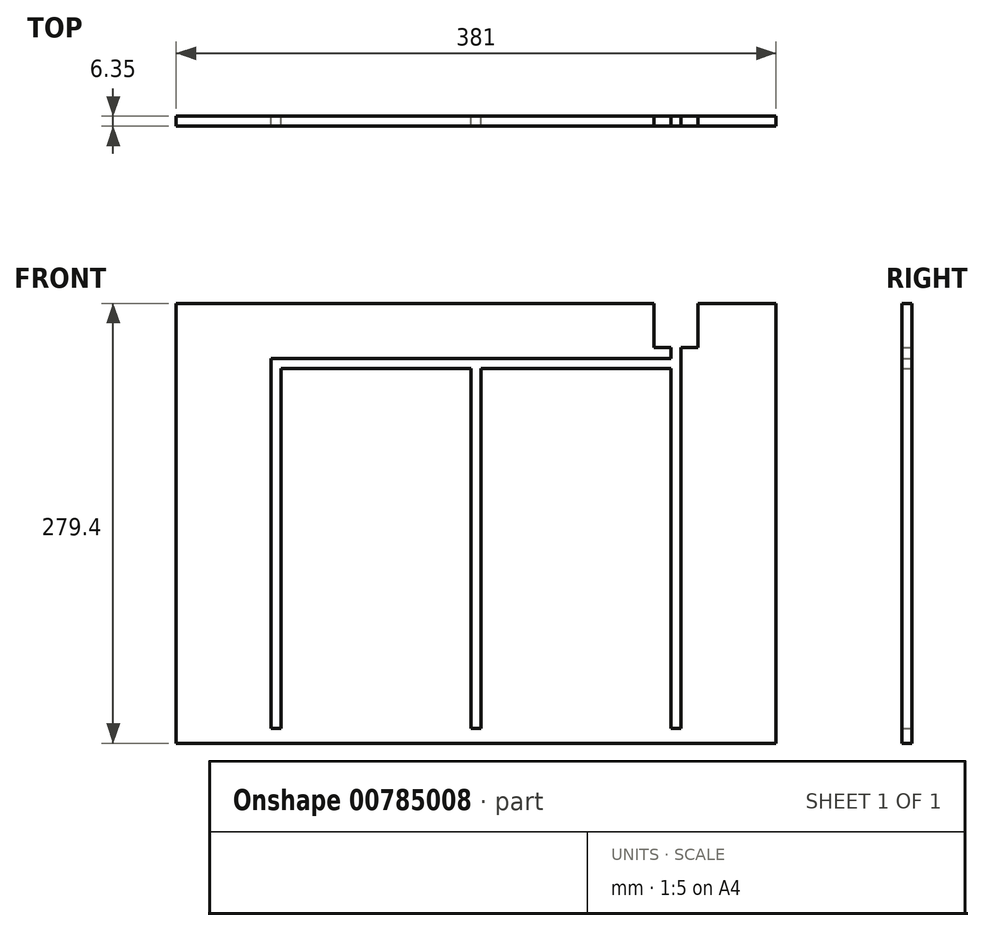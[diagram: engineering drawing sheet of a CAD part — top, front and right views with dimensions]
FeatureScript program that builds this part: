
annotation { "Feature Type Name" : "Feature", "Feature Type Description" : "" }
export const myFeature = defineFeature(function(context is Context, id is Id, definition is map)
    precondition{}
    {
        {
            var Q0;
            Q0=qCreatedBy(makeId("Front.planeOp"),FACE);
            var sketch = newSketch(context, id + "F0", { "sketchPlane" : qUnion([Q0])});
            skLineSegment(sketch, "E0.bottom", {"start": v(-32.74, 42.3) * mm, "end": v(348.26, 42.3) * mm});
            skLineSegment(sketch, "E0.top", {"start": v(-32.74, -237.1) * mm, "end": v(348.26, -237.1) * mm});
            skLineSegment(sketch, "E0.left", {"start": v(-32.74, 42.3) * mm, "end": v(-32.74, -237.1) * mm});
            skLineSegment(sketch, "E0.right", {"start": v(348.26, 42.3) * mm, "end": v(348.26, -237.1) * mm});
            skLineSegment(sketch, "E1.bottom", {"start": v(27.59, 7.37) * mm, "end": v(33.94, 7.37) * mm});
            skLineSegment(sketch, "E1.top", {"start": v(27.59, -227.58) * mm, "end": v(33.94, -227.58) * mm});
            skLineSegment(sketch, "E1.left", {"start": v(27.59, 7.37) * mm, "end": v(27.59, -227.58) * mm});
            skLineSegment(sketch, "E1.right", {"start": v(33.94, 7.37) * mm, "end": v(33.94, -227.58) * mm});
            skPoint(sketch, "E1.middle", {"position": v(30.76, -110.1) * mm});
            skLineSegment(sketch, "E2.bottom", {"start": v(287.94, 7.37) * mm, "end": v(281.59, 7.37) * mm});
            skLineSegment(sketch, "E2.top", {"start": v(287.94, -227.58) * mm, "end": v(281.59, -227.58) * mm});
            skLineSegment(sketch, "E2.left", {"start": v(287.94, 7.37) * mm, "end": v(287.94, -227.58) * mm});
            skLineSegment(sketch, "E2.right", {"start": v(281.59, 7.37) * mm, "end": v(281.59, -227.58) * mm});
            skPoint(sketch, "E2.middle", {"position": v(284.76, -110.1) * mm});
            skLineSegment(sketch, "E3.bottom", {"start": v(154.59, 7.37) * mm, "end": v(160.94, 7.37) * mm});
            skLineSegment(sketch, "E3.top", {"start": v(154.59, -227.58) * mm, "end": v(160.94, -227.58) * mm});
            skLineSegment(sketch, "E3.left", {"start": v(154.59, 7.37) * mm, "end": v(154.59, -227.58) * mm});
            skLineSegment(sketch, "E3.right", {"start": v(160.94, 7.37) * mm, "end": v(160.94, -227.58) * mm});
            skPoint(sketch, "E3.middle", {"position": v(157.76, -110.1) * mm});
            skLineSegment(sketch, "E4", {"start": v(30.76, -110.1) * mm, "end": v(284.76, -110.1) * mm});
            skLineSegment(sketch, "E5.bottom", {"start": v(27.59, 7.37) * mm, "end": v(287.94, 7.37) * mm});
            skLineSegment(sketch, "E5.top", {"start": v(27.59, 1.02) * mm, "end": v(287.94, 1.02) * mm});
            skLineSegment(sketch, "E5.left", {"start": v(27.59, 7.37) * mm, "end": v(27.59, 1.02) * mm});
            skLineSegment(sketch, "E5.right", {"start": v(287.94, 7.37) * mm, "end": v(287.94, 1.02) * mm});
            skLineSegment(sketch, "E6.bottom", {"start": v(281.59, 7.37) * mm, "end": v(287.94, 7.37) * mm});
            skLineSegment(sketch, "E6.top", {"start": v(281.59, 14.36) * mm, "end": v(287.94, 14.36) * mm});
            skLineSegment(sketch, "E6.left", {"start": v(281.59, 7.37) * mm, "end": v(281.59, 14.36) * mm});
            skLineSegment(sketch, "E6.right", {"start": v(287.94, 7.37) * mm, "end": v(287.94, 14.36) * mm});
            skLineSegment(sketch, "E7.bottom", {"start": v(270.8, 42.3) * mm, "end": v(298.73, 42.3) * mm});
            skLineSegment(sketch, "E7.top", {"start": v(270.8, 14.36) * mm, "end": v(298.73, 14.36) * mm});
            skLineSegment(sketch, "E7.left", {"start": v(270.8, 42.3) * mm, "end": v(270.8, 14.36) * mm});
            skLineSegment(sketch, "E7.right", {"start": v(298.73, 42.3) * mm, "end": v(298.73, 14.36) * mm});
            skPoint(sketch, "E7.middle", {"position": v(284.76, 28.33) * mm});
            skSolve(sketch);
        }
        {
            var Q0;
            Q0=makeQuery(id+"F0.imprint","IMPRINT",FACE,{"disambiguationData":[TD([[makeQuery(id+"F0.imprint","IMPRINT",EDGE,{"derivedFrom":sQuery(id+"F0.wireOp",EDGE,"E0.top")}),1.0]])]});
            var Q1;
            {var subQ0=sQuery(id+"F0.wireOp",EDGE,"E4");var subQ1=sQuery(id+"F0.wireOp",EDGE,"E1.right");var subQ2=makeQuery(id+"F0.imprint","INTERSECT",VERTEX,{"derivedFrom":[subQ1,subQ0]});Q1=makeQuery(id+"F0.imprint","IMPRINT",FACE,{"disambiguationData":[TD([[makeQuery(id+"F0.imprint","IMPRINT",EDGE,{"disambiguationData":[TD([[subQ2,1.0]])],"derivedFrom":subQ1}),1.0]])]});}
            var Q2;
            {var subQ0=sQuery(id+"F0.wireOp",EDGE,"E4");var subQ1=sQuery(id+"F0.wireOp",EDGE,"E2.right");var subQ2=makeQuery(id+"F0.imprint","INTERSECT",VERTEX,{"derivedFrom":[subQ1,subQ0]});Q2=makeQuery(id+"F0.imprint","IMPRINT",FACE,{"disambiguationData":[TD([[makeQuery(id+"F0.imprint","IMPRINT",EDGE,{"disambiguationData":[TD([[subQ2,1.0]])],"derivedFrom":subQ1}),-1.0]])]});}
            extrude(context, id + "F1", {"entities" : qUnion([Q0, Q1, Q2]), "depth" : 6.35 * mm, "offsetDistance" : 25.4 * mm});
        }
    });
